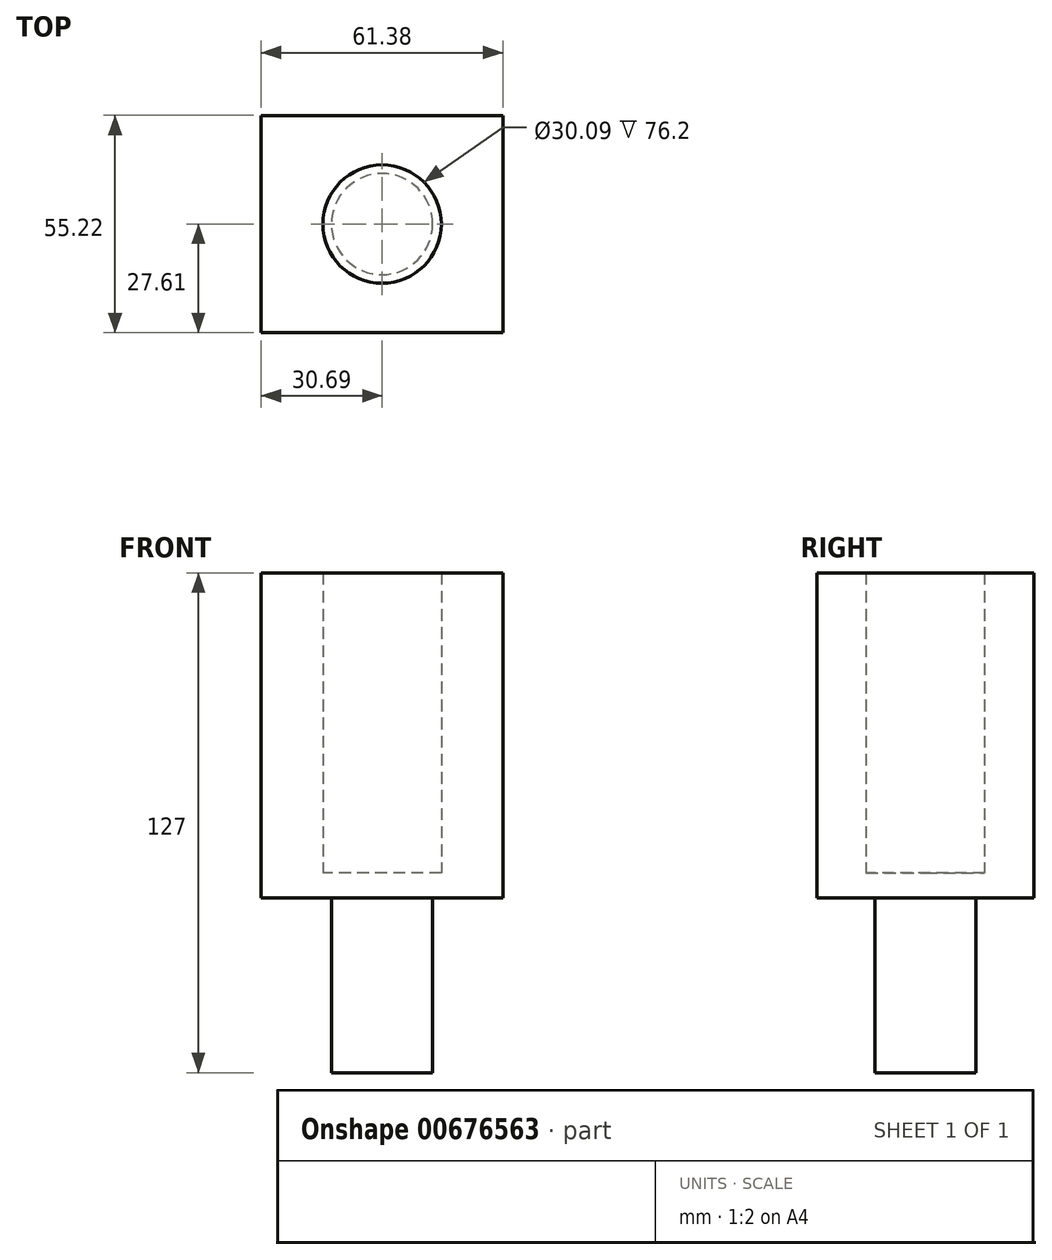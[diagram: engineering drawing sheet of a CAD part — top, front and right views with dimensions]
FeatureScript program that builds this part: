
annotation { "Feature Type Name" : "Feature", "Feature Type Description" : "" }
export const myFeature = defineFeature(function(context is Context, id is Id, definition is map)
    precondition{}
    {
        {
            var Q0;
            Q0=qCreatedBy(makeId("Top.planeOp"),FACE);
            var sketch = newSketch(context, id + "F0", { "sketchPlane" : qUnion([Q0])});
            skCircle(sketch, "E0", {"center": v(0, 0) * mm, "radius": 12.85 * mm});
            skCircle(sketch, "E1", {"center": v(0, 0) * mm, "radius": 15.05 * mm});
            skLineSegment(sketch, "E2.bottom", {"start": v(30.7, 27.6) * mm, "end": v(-30.7, 27.6) * mm});
            skLineSegment(sketch, "E2.top", {"start": v(30.7, -27.6) * mm, "end": v(-30.7, -27.6) * mm});
            skLineSegment(sketch, "E2.left", {"start": v(30.7, 27.6) * mm, "end": v(30.7, -27.6) * mm});
            skLineSegment(sketch, "E2.right", {"start": v(-30.7, 27.6) * mm, "end": v(-30.7, -27.6) * mm});
            skSolve(sketch);
        }
        {
            var Q0;
            Q0=makeQuery(id+"F0.imprint","IMPRINT",FACE,{"disambiguationData":[TD([[makeQuery(id+"F0.imprint","IMPRINT",EDGE,{"derivedFrom":sQuery(id+"F0.wireOp",EDGE,"E1")}),-1.0]])]});
            extrude(context, id + "F1", {"entities" : qUnion([Q0]), "depth" : 76.2 * mm, "offsetDistance" : 25.4 * mm});
        }
        {
            var Q0;
            Q0=makeQuery(id+"F0.imprint","IMPRINT",FACE,{"disambiguationData":[TD([[makeQuery(id+"F0.imprint","IMPRINT",EDGE,{"derivedFrom":sQuery(id+"F0.wireOp",EDGE,"E0")}),1.0]])]});
            extrude(context, id + "F2", {"entities" : qUnion([Q0]), "oppositeDirection" : true, "depth" : 50.8 * mm, "offsetDistance" : 25.4 * mm});
        }
        {
            var Q0;
            Q0=makeQuery(id+"F0.imprint","IMPRINT",FACE,{"disambiguationData":[TD([[makeQuery(id+"F0.imprint","IMPRINT",EDGE,{"derivedFrom":sQuery(id+"F0.wireOp",EDGE,"E1")}),-1.0]])]});
            var Q1;
            Q1=makeQuery(id+"F0.imprint","IMPRINT",FACE,{"disambiguationData":[TD([[makeQuery(id+"F0.imprint","IMPRINT",EDGE,{"derivedFrom":sQuery(id+"F0.wireOp",EDGE,"E0")}),-1.0]])]});
            extrude(context, id + "F3", {"entities" : qUnion([Q0, Q1]), "operationType" : NewBodyOperationType.ADD, "oppositeDirection" : true, "depth" : 6.35 * mm, "offsetDistance" : 25.4 * mm});
        }
    });
